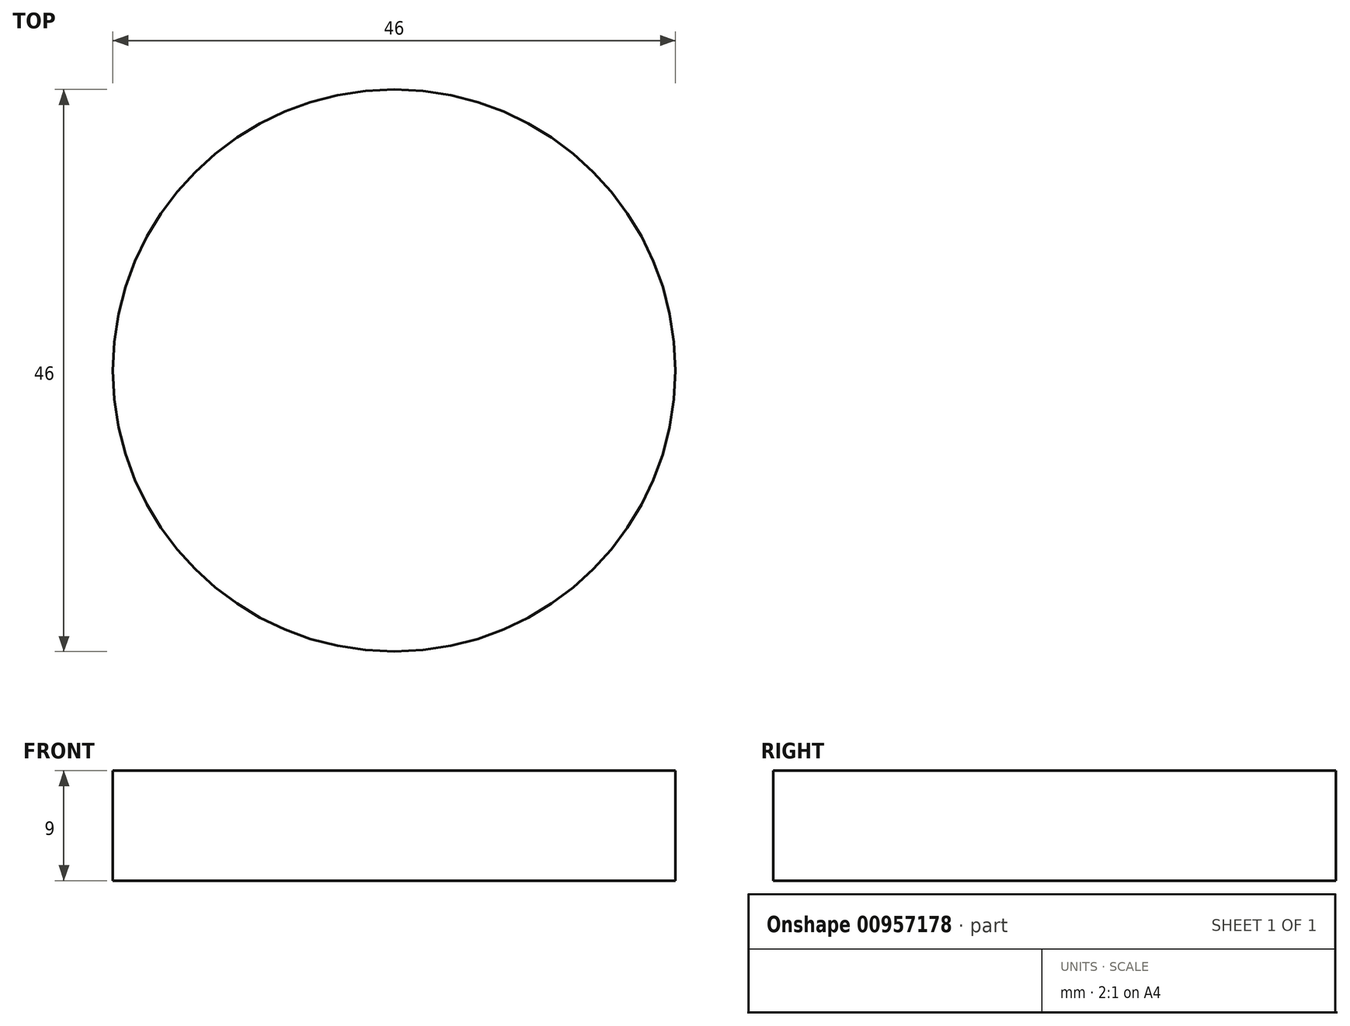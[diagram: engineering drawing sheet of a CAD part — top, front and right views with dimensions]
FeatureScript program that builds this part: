
annotation { "Feature Type Name" : "Feature", "Feature Type Description" : "" }
export const myFeature = defineFeature(function(context is Context, id is Id, definition is map)
    precondition{}
    {
        {
            var Q0;
            Q0=qCreatedBy(makeId("Top.planeOp"), FACE);
            var sketch = newSketch(context, id + "F0", { "sketchPlane" : qUnion([Q0])});
            skCircle(sketch, "E0", {"center": v(0, -2.06) * mm, "radius": 23 * mm});
            skSolve(sketch);
        }
        {
            var Q0;
            Q0 = qSketchRegion(id + "F0", true);
            extrude(context, id + "F1", {"entities" : qUnion([Q0]), "domain" : OperationDomain.MODEL, "flatOperationType" : FlatOperationType.REMOVE, "depth" : 9 * mm, "offsetDistance" : 25 * mm});
        }
    });
